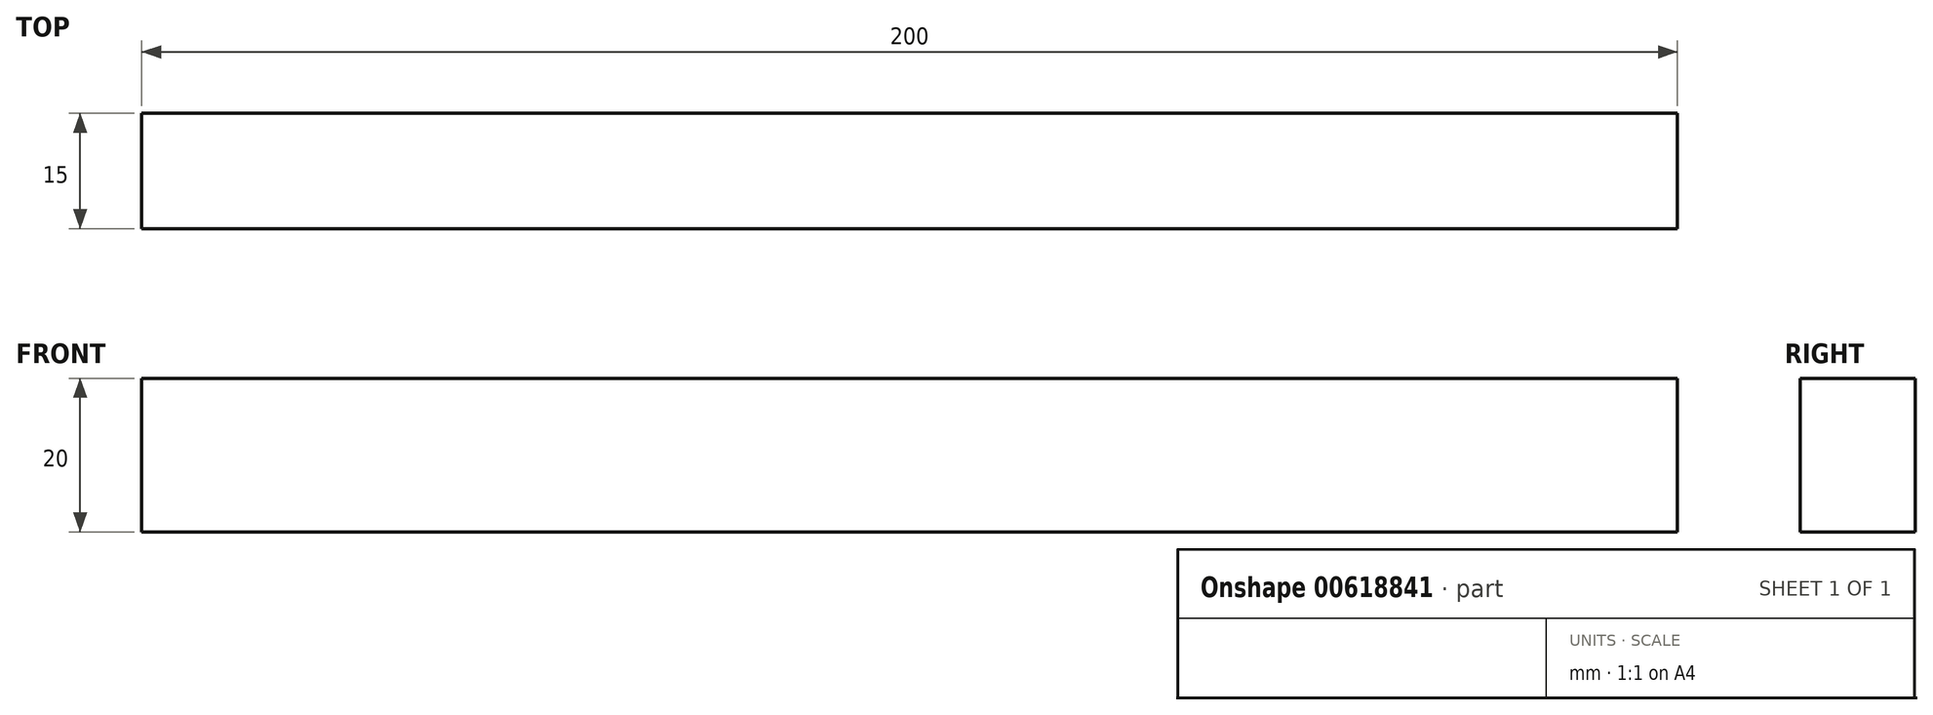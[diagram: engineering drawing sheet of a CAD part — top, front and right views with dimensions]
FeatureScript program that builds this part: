
annotation { "Feature Type Name" : "Feature", "Feature Type Description" : "" }
export const myFeature = defineFeature(function(context is Context, id is Id, definition is map)
    precondition{}
    {
        {
            var Q0;
            Q0=qCreatedBy(makeId("Front.planeOp"),FACE);
            var sketch = newSketch(context, id + "F0", { "sketchPlane" : qUnion([Q0])});
            skLineSegment(sketch, "E0.bottom", {"start": v(-100, 10) * mm, "end": v(100, 10) * mm});
            skLineSegment(sketch, "E0.top", {"start": v(-100, -10) * mm, "end": v(100, -10) * mm});
            skLineSegment(sketch, "E0.left", {"start": v(-100, 10) * mm, "end": v(-100, -10) * mm});
            skLineSegment(sketch, "E0.right", {"start": v(100, 10) * mm, "end": v(100, -10) * mm});
            skPoint(sketch, "E0.middle", {"position": v(0, 0) * mm});
            skSolve(sketch);
        }
        {
            var Q0;
            Q0 = qSketchRegion(id + "F0", true);
            extrude(context, id + "F1", {"entities" : qUnion([Q0]), "depth" : 15 * mm, "offsetDistance" : 25 * mm});
        }
    });
